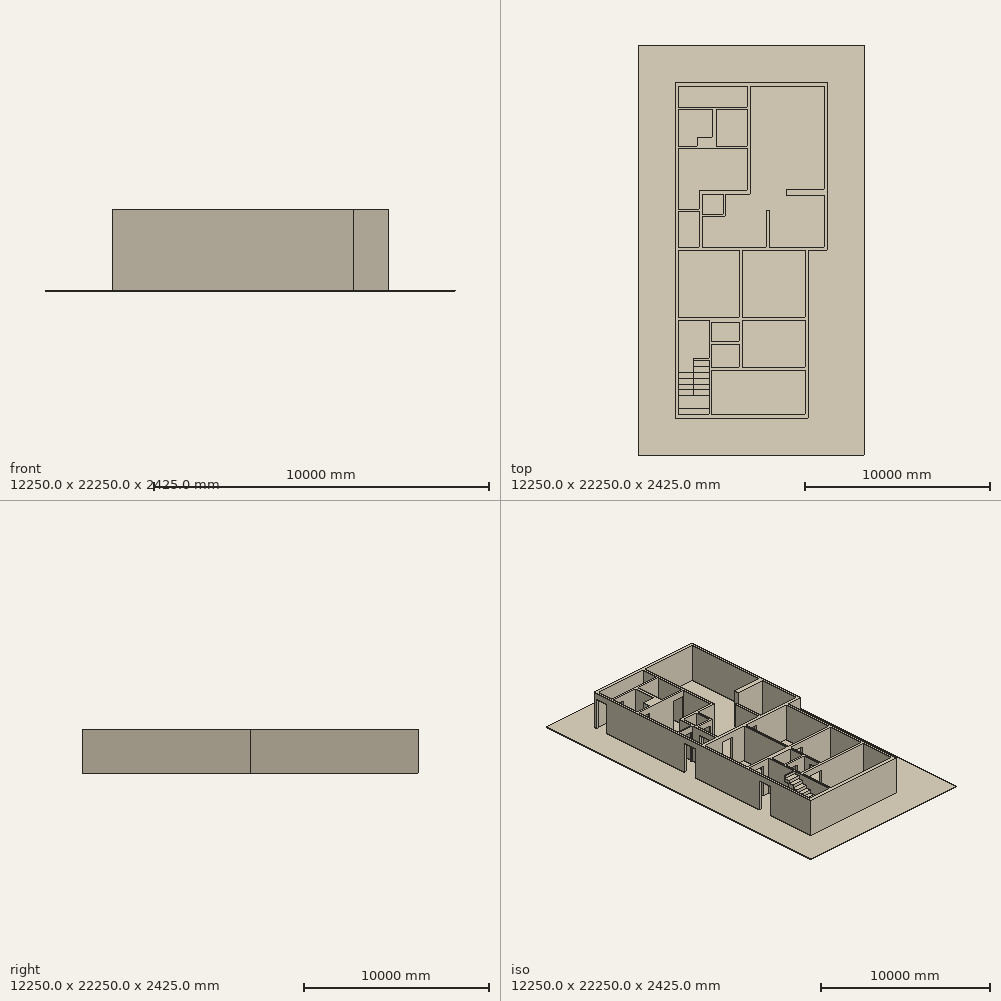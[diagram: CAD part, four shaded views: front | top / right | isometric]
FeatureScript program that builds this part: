
annotation { "Feature Type Name" : "Feature", "Feature Type Description" : "" }
export const myFeature = defineFeature(function(context is Context, id is Id, definition is map)
    precondition{}
    {
        {
            var Q0;
            Q0=qCreatedBy(makeId("Top.planeOp"),FACE);
            var sketch = newSketch(context, id + "F0", { "sketchPlane" : qUnion([Q0])});
            skLineSegment(sketch, "E0.bottom", {"start": v(-4125, 0) * mm, "end": v(4125, 0) * mm});
            skLineSegment(sketch, "E0.top", {"start": v(-3955, -9150) * mm, "end": v(-655, -9150) * mm});
            skLineSegment(sketch, "E0.left", {"start": v(-4125, 0) * mm, "end": v(-4125, -9150) * mm});
            skLineSegment(sketch, "E0.right", {"start": v(4125, 0) * mm, "end": v(4125, -9150) * mm});
            skLineSegment(sketch, "E1.bottom", {"start": v(-4125, -18250) * mm, "end": v(3075, -18250) * mm});
            skLineSegment(sketch, "E1.left", {"start": v(-4125, -18250) * mm, "end": v(-4125, -9150) * mm});
            skLineSegment(sketch, "E1.right", {"start": v(3075, -18250) * mm, "end": v(3075, -9150) * mm});
            skLineSegment(sketch, "E2.bottom", {"start": v(-3955, -200) * mm, "end": v(-195, -200) * mm});
            skLineSegment(sketch, "E2.top", {"start": v(-3955, -1340) * mm, "end": v(-195, -1340) * mm});
            skLineSegment(sketch, "E2.left", {"start": v(-3955, -200) * mm, "end": v(-3955, -1340) * mm});
            skLineSegment(sketch, "E2.right", {"start": v(-195, -200) * mm, "end": v(-195, -1340) * mm});
            skLineSegment(sketch, "E3.bottom", {"start": v(-3955, -1490) * mm, "end": v(-2105, -1490) * mm});
            skLineSegment(sketch, "E3.top", {"start": v(-3955, -3500) * mm, "end": v(-2105, -3500) * mm});
            skLineSegment(sketch, "E3.left", {"start": v(-3955, -1490) * mm, "end": v(-3955, -3500) * mm});
            skLineSegment(sketch, "E3.right", {"start": v(-2105, -1490) * mm, "end": v(-2105, -3500) * mm});
            skLineSegment(sketch, "E4.bottom", {"start": v(-1905, -1490) * mm, "end": v(-195, -1490) * mm});
            skLineSegment(sketch, "E4.top", {"start": v(-1905, -3500) * mm, "end": v(-195, -3500) * mm});
            skLineSegment(sketch, "E4.left", {"start": v(-1905, -1490) * mm, "end": v(-1905, -3500) * mm});
            skLineSegment(sketch, "E5.bottom", {"start": v(-3955, -3615) * mm, "end": v(-195, -3615) * mm});
            skLineSegment(sketch, "E5.top", {"start": v(-2825, -5885) * mm, "end": v(-195, -5885) * mm});
            skLineSegment(sketch, "E5.left", {"start": v(-3955, -3615) * mm, "end": v(-3955, -5885) * mm});
            skLineSegment(sketch, "E5.right", {"start": v(-195, -3615) * mm, "end": v(-195, -5885) * mm});
            skLineSegment(sketch, "E6.bottom", {"start": v(-2825, -6885) * mm, "end": v(-3955, -6885) * mm});
            skLineSegment(sketch, "E6.left", {"start": v(-2825, -6885) * mm, "end": v(-2825, -5885) * mm});
            skLineSegment(sketch, "E6.right", {"start": v(-3955, -6885) * mm, "end": v(-3955, -5885) * mm});
            skLineSegment(sketch, "E7.bottom", {"start": v(-3955, -8950) * mm, "end": v(-2825, -8950) * mm});
            skLineSegment(sketch, "E7.top", {"start": v(-3955, -7000) * mm, "end": v(-2825, -7000) * mm});
            skLineSegment(sketch, "E7.left", {"start": v(-3955, -8950) * mm, "end": v(-3955, -7000) * mm});
            skLineSegment(sketch, "E7.right", {"start": v(-2825, -8950) * mm, "end": v(-2825, -7000) * mm});
            skLineSegment(sketch, "E8.bottom", {"start": v(-2665, -6070) * mm, "end": v(-1545, -6070) * mm});
            skLineSegment(sketch, "E8.top", {"start": v(-2665, -7170) * mm, "end": v(-1545, -7170) * mm});
            skLineSegment(sketch, "E8.left", {"start": v(-2665, -6070) * mm, "end": v(-2665, -7170) * mm});
            skLineSegment(sketch, "E8.right", {"start": v(-1545, -6070) * mm, "end": v(-1545, -7170) * mm});
            skLineSegment(sketch, "E9.bottom", {"start": v(-45, -200) * mm, "end": v(3955, -200) * mm});
            skLineSegment(sketch, "E9.top", {"start": v(1905, -5800) * mm, "end": v(3955, -5800) * mm});
            skLineSegment(sketch, "E9.right", {"start": v(3955, -200) * mm, "end": v(3955, -5800) * mm});
            skLineSegment(sketch, "E10.bottom", {"start": v(3955, -8950) * mm, "end": v(955, -8950) * mm});
            skLineSegment(sketch, "E10.top", {"start": v(3955, -6120) * mm, "end": v(1905, -6120) * mm});
            skLineSegment(sketch, "E10.left", {"start": v(3955, -8950) * mm, "end": v(3955, -6120) * mm});
            skLineSegment(sketch, "E10.right", {"start": v(955, -8950) * mm, "end": v(955, -6950) * mm});
            skLineSegment(sketch, "E11.bottom", {"start": v(805, -8950) * mm, "end": v(-2665, -8950) * mm});
            skLineSegment(sketch, "E11.top", {"start": v(-1415, -7270) * mm, "end": v(-2665, -7270) * mm});
            skLineSegment(sketch, "E11.right", {"start": v(-2665, -8950) * mm, "end": v(-2665, -7270) * mm});
            skLineSegment(sketch, "E12.left", {"start": v(-1415, -6070) * mm, "end": v(-1415, -7270) * mm});
            skLineSegment(sketch, "E13.top", {"start": v(-3955, -18000) * mm, "end": v(-2305, -18000) * mm});
            skLineSegment(sketch, "E14.bottom", {"start": v(-2175, -15650) * mm, "end": v(2905, -15650) * mm});
            skLineSegment(sketch, "E14.top", {"start": v(-2175, -18000) * mm, "end": v(2905, -18000) * mm});
            skLineSegment(sketch, "E14.left", {"start": v(-2175, -15650) * mm, "end": v(-2175, -18000) * mm});
            skLineSegment(sketch, "E14.right", {"start": v(2905, -15650) * mm, "end": v(2905, -18000) * mm});
            skLineSegment(sketch, "E15.bottom", {"start": v(-2175, -13050) * mm, "end": v(-625, -13050) * mm});
            skLineSegment(sketch, "E15.top", {"start": v(-2175, -14085) * mm, "end": v(-625, -14085) * mm});
            skLineSegment(sketch, "E15.left", {"start": v(-2175, -13050) * mm, "end": v(-2175, -14085) * mm});
            skLineSegment(sketch, "E15.right", {"start": v(-625, -13050) * mm, "end": v(-625, -14085) * mm});
            skLineSegment(sketch, "E16.bottom", {"start": v(-2175, -14200) * mm, "end": v(-625, -14200) * mm});
            skLineSegment(sketch, "E16.top", {"start": v(-2175, -15500) * mm, "end": v(-625, -15500) * mm});
            skLineSegment(sketch, "E16.left", {"start": v(-2175, -14200) * mm, "end": v(-2175, -15500) * mm});
            skLineSegment(sketch, "E16.right", {"start": v(-625, -14200) * mm, "end": v(-625, -15500) * mm});
            skLineSegment(sketch, "E17.bottom", {"start": v(-495, -12900) * mm, "end": v(2905, -12900) * mm});
            skLineSegment(sketch, "E17.top", {"start": v(-495, -15500) * mm, "end": v(2905, -15500) * mm});
            skLineSegment(sketch, "E17.left", {"start": v(-495, -12900) * mm, "end": v(-495, -15500) * mm});
            skLineSegment(sketch, "E17.right", {"start": v(2905, -12900) * mm, "end": v(2905, -15500) * mm});
            skLineSegment(sketch, "E18.bottom", {"start": v(-3955, -12900) * mm, "end": v(-2305, -12900) * mm});
            skLineSegment(sketch, "E19.bottom", {"start": v(-3955, -12750) * mm, "end": v(-655, -12750) * mm});
            skLineSegment(sketch, "E19.left", {"start": v(-3955, -12750) * mm, "end": v(-3955, -9150) * mm});
            skLineSegment(sketch, "E19.right", {"start": v(-655, -12750) * mm, "end": v(-655, -9150) * mm});
            skLineSegment(sketch, "E20.bottom", {"start": v(-495, -12750) * mm, "end": v(2905, -12750) * mm});
            skLineSegment(sketch, "E20.top", {"start": v(-495, -9150) * mm, "end": v(2905, -9150) * mm});
            skLineSegment(sketch, "E20.left", {"start": v(-495, -12750) * mm, "end": v(-495, -9150) * mm});
            skLineSegment(sketch, "E20.right", {"start": v(2905, -12750) * mm, "end": v(2905, -9150) * mm});
            skLineSegment(sketch, "E21.trimOffspring", {"start": v(-495, -9150) * mm, "end": v(3075, -9150) * mm});
            skLineSegment(sketch, "E22.trimOffspring", {"start": v(-495, -9150) * mm, "end": v(4125, -9150) * mm});
            skLineSegment(sketch, "E23", {"start": v(-2955, -3500) * mm, "end": v(-2955, -2970) * mm});
            skLineSegment(sketch, "E24", {"start": v(-2955, -2970) * mm, "end": v(-2105, -2970) * mm});
            skLineSegment(sketch, "E25", {"start": v(-195, -1490) * mm, "end": v(-195, -3500) * mm});
            skLineSegment(sketch, "E26", {"start": v(805, -8950) * mm, "end": v(805, -6950) * mm});
            skLineSegment(sketch, "E27", {"start": v(805, -6950) * mm, "end": v(955, -6950) * mm});
            skLineSegment(sketch, "E28", {"start": v(1905, -6120) * mm, "end": v(1905, -5800) * mm});
            skLineSegment(sketch, "E29", {"start": v(-1415, -6070) * mm, "end": v(-45, -6070) * mm});
            skLineSegment(sketch, "E30", {"start": v(-45, -6070) * mm, "end": v(-45, -200) * mm});
            skLineSegment(sketch, "E31", {"start": v(-2305, -12900) * mm, "end": v(-2305, -18000) * mm});
            skLineSegment(sketch, "E32", {"start": v(-3955, -18000) * mm, "end": v(-3955, -12900) * mm});
            skPoint(sketch, "E33.endSnap0", {"position": v(-3130, -18000) * mm});
            skSolve(sketch);
        }
        {
            var Q0;
            Q0=makeQuery(id+"F0.imprint","IMPRINT",FACE,{"disambiguationData":[TD([[makeQuery(id+"F0.imprint","IMPRINT",EDGE,{"derivedFrom":sQuery(id+"F0.wireOp",EDGE,"E0.bottom")}),-1.0]])]});
            var Q1;
            {var subQ3=sQuery(id+"F0.wireOp",EDGE,"E23");Q1=makeQuery(id+"F0.imprint","IMPRINT",FACE,{"disambiguationData":[TD([[makeQuery(id+"F0.imprint","IMPRINT",EDGE,{"derivedFrom":subQ3}),-1.0]])]});}
            extrude(context, id + "F1", {"entities" : qUnion([Q0, Q1]), "depth" : 2400 * mm});
        }
        {
            var Q0;
            Q0=makeQuery(id+"F1.opExtrude","CAP_FACE",FACE,{"disambiguationData":[OSD([sQuery(id+"F0.wireOp",EDGE,"E0.bottom"),sQuery(id+"F0.wireOp",EDGE,"E0.left"),sQuery(id+"F0.wireOp",EDGE,"E0.right"),sQuery(id+"F0.wireOp",EDGE,"E1.bottom"),sQuery(id+"F0.wireOp",EDGE,"E1.left"),sQuery(id+"F0.wireOp",EDGE,"E1.right"),sQuery(id+"F0.wireOp",EDGE,"E2.bottom"),sQuery(id+"F0.wireOp",EDGE,"E2.top"),sQuery(id+"F0.wireOp",EDGE,"E2.left"),sQuery(id+"F0.wireOp",EDGE,"E2.right"),sQuery(id+"F0.wireOp",EDGE,"E3.bottom"),sQuery(id+"F0.wireOp",EDGE,"E3.top"),sQuery(id+"F0.wireOp",EDGE,"E3.left"),sQuery(id+"F0.wireOp",EDGE,"E3.right"),sQuery(id+"F0.wireOp",EDGE,"E4.bottom"),sQuery(id+"F0.wireOp",EDGE,"E4.top"),sQuery(id+"F0.wireOp",EDGE,"E4.left"),sQuery(id+"F0.wireOp",EDGE,"E5.bottom"),sQuery(id+"F0.wireOp",EDGE,"E5.top"),sQuery(id+"F0.wireOp",EDGE,"E5.left"),sQuery(id+"F0.wireOp",EDGE,"E5.right"),sQuery(id+"F0.wireOp",EDGE,"E6.bottom"),sQuery(id+"F0.wireOp",EDGE,"E6.left"),sQuery(id+"F0.wireOp",EDGE,"E6.right"),sQuery(id+"F0.wireOp",EDGE,"E7.bottom"),sQuery(id+"F0.wireOp",EDGE,"E7.top"),sQuery(id+"F0.wireOp",EDGE,"E7.left"),sQuery(id+"F0.wireOp",EDGE,"E7.right"),sQuery(id+"F0.wireOp",EDGE,"E8.bottom"),sQuery(id+"F0.wireOp",EDGE,"E8.top"),sQuery(id+"F0.wireOp",EDGE,"E8.left"),sQuery(id+"F0.wireOp",EDGE,"E8.right"),sQuery(id+"F0.wireOp",EDGE,"E9.bottom"),sQuery(id+"F0.wireOp",EDGE,"E9.top"),sQuery(id+"F0.wireOp",EDGE,"E9.right"),sQuery(id+"F0.wireOp",EDGE,"E10.bottom"),sQuery(id+"F0.wireOp",EDGE,"E10.top"),sQuery(id+"F0.wireOp",EDGE,"E10.left"),sQuery(id+"F0.wireOp",EDGE,"E10.right"),sQuery(id+"F0.wireOp",EDGE,"E11.bottom"),sQuery(id+"F0.wireOp",EDGE,"E11.top"),sQuery(id+"F0.wireOp",EDGE,"E11.right"),sQuery(id+"F0.wireOp",EDGE,"E12.left"),sQuery(id+"F0.wireOp",EDGE,"E13.bottom"),sQuery(id+"F0.wireOp",EDGE,"E13.top"),sQuery(id+"F0.wireOp",EDGE,"E13.left"),sQuery(id+"F0.wireOp",EDGE,"E13.right"),sQuery(id+"F0.wireOp",EDGE,"E14.bottom"),sQuery(id+"F0.wireOp",EDGE,"E14.top"),sQuery(id+"F0.wireOp",EDGE,"E14.left"),sQuery(id+"F0.wireOp",EDGE,"E14.right"),sQuery(id+"F0.wireOp",EDGE,"E15.bottom"),sQuery(id+"F0.wireOp",EDGE,"E15.top"),sQuery(id+"F0.wireOp",EDGE,"E15.left"),sQuery(id+"F0.wireOp",EDGE,"E15.right"),sQuery(id+"F0.wireOp",EDGE,"E16.bottom"),sQuery(id+"F0.wireOp",EDGE,"E16.top"),sQuery(id+"F0.wireOp",EDGE,"E16.left"),sQuery(id+"F0.wireOp",EDGE,"E16.right"),sQuery(id+"F0.wireOp",EDGE,"E17.bottom"),sQuery(id+"F0.wireOp",EDGE,"E17.top"),sQuery(id+"F0.wireOp",EDGE,"E17.left"),sQuery(id+"F0.wireOp",EDGE,"E17.right"),sQuery(id+"F0.wireOp",EDGE,"E18.bottom"),sQuery(id+"F0.wireOp",EDGE,"E18.top"),sQuery(id+"F0.wireOp",EDGE,"E18.left"),sQuery(id+"F0.wireOp",EDGE,"E18.right"),sQuery(id+"F0.wireOp",EDGE,"E19.bottom"),sQuery(id+"F0.wireOp",EDGE,"E0.top"),sQuery(id+"F0.wireOp",EDGE,"E19.left"),sQuery(id+"F0.wireOp",EDGE,"E19.right"),sQuery(id+"F0.wireOp",EDGE,"E20.bottom"),sQuery(id+"F0.wireOp",EDGE,"E20.left"),sQuery(id+"F0.wireOp",EDGE,"E20.right"),sQuery(id+"F0.wireOp",EDGE,"E22.trimOffspring"),sQuery(id+"F0.wireOp",EDGE,"E25"),sQuery(id+"F0.wireOp",EDGE,"E26"),sQuery(id+"F0.wireOp",EDGE,"E27"),sQuery(id+"F0.wireOp",EDGE,"E28"),sQuery(id+"F0.wireOp",EDGE,"E29"),sQuery(id+"F0.wireOp",EDGE,"E30")])],"isStart":false});
            var sketch = newSketch(context, id + "F2", { "sketchPlane" : qUnion([Q0])});
            skLineSegment(sketch, "E34", {"start": v(-1575, -15500) * mm, "end": v(-1575, -15650) * mm});
            skLineSegment(sketch, "E35", {"start": v(-1575, -15650) * mm, "end": v(-675, -15650) * mm});
            skLineSegment(sketch, "E36", {"start": v(-675, -15650) * mm, "end": v(-675, -15500) * mm});
            skLineSegment(sketch, "E37", {"start": v(-625, -15480) * mm, "end": v(-495, -15480) * mm});
            skLineSegment(sketch, "E38", {"start": v(-495, -14600) * mm, "end": v(-625, -14600) * mm});
            skLineSegment(sketch, "E39", {"start": v(-2175, -15400) * mm, "end": v(-2305, -15400) * mm});
            skLineSegment(sketch, "E40", {"start": v(-2025, -14200) * mm, "end": v(-2025, -14085) * mm});
            skLineSegment(sketch, "E41", {"start": v(-2025, -14085) * mm, "end": v(-1225, -14085) * mm});
            skLineSegment(sketch, "E42", {"start": v(-1225, -14085) * mm, "end": v(-1225, -14200) * mm});
            skLineSegment(sketch, "E43", {"start": v(-345, -12750) * mm, "end": v(-345, -12900) * mm});
            skLineSegment(sketch, "E44", {"start": v(-345, -12900) * mm, "end": v(505, -12900) * mm});
            skLineSegment(sketch, "E45", {"start": v(505, -12900) * mm, "end": v(505, -12750) * mm});
            skLineSegment(sketch, "E46", {"start": v(-445, -8950) * mm, "end": v(-445, -9150) * mm});
            skLineSegment(sketch, "E47", {"start": v(-445, -9150) * mm, "end": v(405, -9150) * mm});
            skLineSegment(sketch, "E48", {"start": v(405, -9150) * mm, "end": v(405, -8950) * mm});
            skLineSegment(sketch, "E49", {"start": v(-1615, -8950) * mm, "end": v(-1615, -9150) * mm});
            skLineSegment(sketch, "E50", {"start": v(-1615, -9150) * mm, "end": v(-2465, -9150) * mm});
            skLineSegment(sketch, "E51", {"start": v(-2465, -9150) * mm, "end": v(-2465, -8950) * mm});
            skLineSegment(sketch, "E52", {"start": v(-2665, -7570) * mm, "end": v(-2825, -7570) * mm});
            skLineSegment(sketch, "E53", {"start": v(-2825, -7570) * mm, "end": v(-2825, -8450) * mm});
            skLineSegment(sketch, "E54", {"start": v(-2825, -8450) * mm, "end": v(-2665, -8450) * mm});
            skLineSegment(sketch, "E55", {"start": v(-2215, -7170) * mm, "end": v(-2215, -7270) * mm});
            skLineSegment(sketch, "E56", {"start": v(-2215, -7270) * mm, "end": v(-1565, -7270) * mm});
            skLineSegment(sketch, "E57", {"start": v(-1565, -7270) * mm, "end": v(-1565, -7170) * mm});
            skLineSegment(sketch, "E58", {"start": v(-3755, -6885) * mm, "end": v(-3755, -7000) * mm});
            skLineSegment(sketch, "E59", {"start": v(-3755, -7000) * mm, "end": v(-2905, -7000) * mm});
            skLineSegment(sketch, "E60", {"start": v(-2905, -7000) * mm, "end": v(-2905, -6885) * mm});
            skLineSegment(sketch, "E61", {"start": v(-3655, -12750) * mm, "end": v(-3655, -12900) * mm});
            skLineSegment(sketch, "E62", {"start": v(-3655, -12900) * mm, "end": v(-2805, -12900) * mm});
            skLineSegment(sketch, "E63", {"start": v(-2805, -12900) * mm, "end": v(-2805, -12750) * mm});
            skLineSegment(sketch, "E64", {"start": v(-205, -3500) * mm, "end": v(-205, -3615) * mm});
            skLineSegment(sketch, "E65", {"start": v(-205, -3615) * mm, "end": v(-1075, -3615) * mm});
            skLineSegment(sketch, "E66", {"start": v(-1075, -3615) * mm, "end": v(-1075, -3500) * mm});
            skLineSegment(sketch, "E67", {"start": v(-3935, -3500) * mm, "end": v(-3935, -3615) * mm});
            skLineSegment(sketch, "E68", {"start": v(-3935, -3615) * mm, "end": v(-3055, -3615) * mm});
            skLineSegment(sketch, "E69", {"start": v(-3055, -3615) * mm, "end": v(-3055, -1490) * mm});
            skLineSegment(sketch, "E70", {"start": v(-3935, -1340) * mm, "end": v(-3935, -1490) * mm});
            skLineSegment(sketch, "E71", {"start": v(-3935, -1490) * mm, "end": v(-3135, -1490) * mm});
            skLineSegment(sketch, "E72", {"start": v(-3135, -1490) * mm, "end": v(-3135, -1340) * mm});
            skLineSegment(sketch, "E73", {"start": v(-4125, -7620) * mm, "end": v(-3955, -7620) * mm});
            skLineSegment(sketch, "E74", {"start": v(-3955, -7620) * mm, "end": v(-3955, -8500) * mm});
            skLineSegment(sketch, "E75", {"start": v(-3955, -8500) * mm, "end": v(-4125, -8500) * mm});
            skLineSegment(sketch, "E76", {"start": v(-3955, -240) * mm, "end": v(-4125, -240) * mm});
            skLineSegment(sketch, "E77", {"start": v(-4125, -240) * mm, "end": v(-4125, -1090) * mm});
            skLineSegment(sketch, "E78", {"start": v(-4125, -1090) * mm, "end": v(-3955, -1090) * mm});
            skLineSegment(sketch, "E79", {"start": v(-2305, -14520) * mm, "end": v(-2175, -14520) * mm});
            skLineSegment(sketch, "E80", {"start": v(-2175, -14520) * mm, "end": v(-2175, -15400) * mm});
            skLineSegment(sketch, "E81", {"start": v(-4125, -13950) * mm, "end": v(-3955, -13950) * mm});
            skLineSegment(sketch, "E82", {"start": v(-3955, -13950) * mm, "end": v(-3955, -14830) * mm});
            skLineSegment(sketch, "E83", {"start": v(-3955, -14830) * mm, "end": v(-4125, -14830) * mm});
            skSolve(sketch);
        }
        {
            var Q0;
            {var subQ0=sQuery(id+"F2.wireOp",EDGE,"E76");Q0=makeQuery(id+"F2.imprint","IMPRINT",FACE,{"disambiguationData":[TD([[makeQuery(id+"F2.imprint","IMPRINT",EDGE,{"derivedFrom":subQ0}),1.0]])]});}
            var Q1;
            {var subQ0=sQuery(id+"F2.wireOp",EDGE,"E70");Q1=makeQuery(id+"F2.imprint","IMPRINT",FACE,{"disambiguationData":[TD([[makeQuery(id+"F2.imprint","IMPRINT",EDGE,{"derivedFrom":subQ0}),1.0]])]});}
            var Q2;
            {var subQ0=sQuery(id+"F2.wireOp",EDGE,"E67");Q2=makeQuery(id+"F2.imprint","IMPRINT",FACE,{"disambiguationData":[TD([[makeQuery(id+"F2.imprint","IMPRINT",EDGE,{"derivedFrom":subQ0}),1.0]])]});}
            var Q3;
            {var subQ0=sQuery(id+"F2.wireOp",EDGE,"E64");Q3=makeQuery(id+"F2.imprint","IMPRINT",FACE,{"disambiguationData":[TD([[makeQuery(id+"F2.imprint","IMPRINT",EDGE,{"derivedFrom":subQ0}),-1.0]])]});}
            var Q4;
            {var subQ0=sQuery(id+"F2.wireOp",EDGE,"E58");Q4=makeQuery(id+"F2.imprint","IMPRINT",FACE,{"disambiguationData":[TD([[makeQuery(id+"F2.imprint","IMPRINT",EDGE,{"derivedFrom":subQ0}),1.0]])]});}
            var Q5;
            {var subQ0=sQuery(id+"F2.wireOp",EDGE,"E73");Q5=makeQuery(id+"F2.imprint","IMPRINT",FACE,{"disambiguationData":[TD([[makeQuery(id+"F2.imprint","IMPRINT",EDGE,{"derivedFrom":subQ0}),-1.0]])]});}
            var Q6;
            {var subQ0=sQuery(id+"F2.wireOp",EDGE,"E55");Q6=makeQuery(id+"F2.imprint","IMPRINT",FACE,{"disambiguationData":[TD([[makeQuery(id+"F2.imprint","IMPRINT",EDGE,{"derivedFrom":subQ0}),1.0]])]});}
            var Q7;
            {var subQ0=sQuery(id+"F2.wireOp",EDGE,"E52");Q7=makeQuery(id+"F2.imprint","IMPRINT",FACE,{"disambiguationData":[TD([[makeQuery(id+"F2.imprint","IMPRINT",EDGE,{"derivedFrom":subQ0}),1.0]])]});}
            var Q8;
            {var subQ0=sQuery(id+"F2.wireOp",EDGE,"E49");Q8=makeQuery(id+"F2.imprint","IMPRINT",FACE,{"disambiguationData":[TD([[makeQuery(id+"F2.imprint","IMPRINT",EDGE,{"derivedFrom":subQ0}),-1.0]])]});}
            var Q9;
            {var subQ0=sQuery(id+"F2.wireOp",EDGE,"E46");Q9=makeQuery(id+"F2.imprint","IMPRINT",FACE,{"disambiguationData":[TD([[makeQuery(id+"F2.imprint","IMPRINT",EDGE,{"derivedFrom":subQ0}),1.0]])]});}
            var Q10;
            {var subQ0=sQuery(id+"F2.wireOp",EDGE,"E61");Q10=makeQuery(id+"F2.imprint","IMPRINT",FACE,{"disambiguationData":[TD([[makeQuery(id+"F2.imprint","IMPRINT",EDGE,{"derivedFrom":subQ0}),1.0]])]});}
            var Q11;
            {var subQ0=sQuery(id+"F2.wireOp",EDGE,"E43");Q11=makeQuery(id+"F2.imprint","IMPRINT",FACE,{"disambiguationData":[TD([[makeQuery(id+"F2.imprint","IMPRINT",EDGE,{"derivedFrom":subQ0}),1.0]])]});}
            var Q12;
            {var subQ0=sQuery(id+"F2.wireOp",EDGE,"E40");Q12=makeQuery(id+"F2.imprint","IMPRINT",FACE,{"disambiguationData":[TD([[makeQuery(id+"F2.imprint","IMPRINT",EDGE,{"derivedFrom":subQ0}),-1.0]])]});}
            var Q13;
            {var subQ0=sQuery(id+"F2.wireOp",EDGE,"E37");Q13=makeQuery(id+"F2.imprint","IMPRINT",FACE,{"disambiguationData":[TD([[makeQuery(id+"F2.imprint","IMPRINT",EDGE,{"derivedFrom":subQ0}),1.0]])]});}
            var Q14;
            {var subQ0=sQuery(id+"F2.wireOp",EDGE,"E34");Q14=makeQuery(id+"F2.imprint","IMPRINT",FACE,{"disambiguationData":[TD([[makeQuery(id+"F2.imprint","IMPRINT",EDGE,{"derivedFrom":subQ0}),1.0]])]});}
            var Q15;
            {var subQ0=sQuery(id+"F2.wireOp",EDGE,"E39");Q15=makeQuery(id+"F2.imprint","IMPRINT",FACE,{"disambiguationData":[TD([[makeQuery(id+"F2.imprint","IMPRINT",EDGE,{"derivedFrom":subQ0}),-1.0]])]});}
            var Q16;
            {var subQ0=sQuery(id+"F2.wireOp",EDGE,"E81");Q16=makeQuery(id+"F2.imprint","IMPRINT",FACE,{"disambiguationData":[TD([[makeQuery(id+"F2.imprint","IMPRINT",EDGE,{"derivedFrom":subQ0}),-1.0]])]});}
            extrude(context, id + "F3", {"entities" : qUnion([Q0, Q1, Q2, Q3, Q4, Q5, Q6, Q7, Q8, Q9, Q10, Q11, Q12, Q13, Q14, Q15, Q16]), "operationType" : NewBodyOperationType.REMOVE, "endBound" : BoundingType.UP_TO_NEXT, "oppositeDirection" : true, "depth" : 2200 * mm, "hasSecondDirection" : true, "secondDirectionOppositeDirection" : true, "secondDirectionDepth" : 400 * mm});
        }
        {
            var Q0;
            Q0=qCreatedBy(makeId("Top.planeOp"),FACE);
            var sketch = newSketch(context, id + "F4", { "sketchPlane" : qUnion([Q0])});
            skLineSegment(sketch, "E84.bottom", {"start": v(6125, -20250) * mm, "end": v(-6125, -20250) * mm});
            skLineSegment(sketch, "E84.top", {"start": v(6125, 2000) * mm, "end": v(-6125, 2000) * mm});
            skLineSegment(sketch, "E84.left", {"start": v(6125, -20250) * mm, "end": v(6125, 2000) * mm});
            skLineSegment(sketch, "E84.right", {"start": v(-6125, -20250) * mm, "end": v(-6125, 2000) * mm});
            skSolve(sketch);
        }
        {
            var Q0;
            Q0 = qSketchRegion(id + "F4", true);
            extrude(context, id + "F5", {"entities" : qUnion([Q0]), "oppositeDirection" : true, "depth" : 25 * mm});
        }
        {
            var Q0;
            Q0=makeQuery(id+"F1.opExtrude","SWEPT_FACE",FACE,{"disambiguationData":[OSD([sQuery(id+"F0.wireOp",EDGE,"E31")])]});
            var sketch = newSketch(context, id + "F6", { "sketchPlane" : qUnion([Q0])});
            skLineSegment(sketch, "E85", {"start": v(15730, 220) * mm, "end": v(16050, 220) * mm});
            skLineSegment(sketch, "E86", {"start": v(16050, 220) * mm, "end": v(16050, 420) * mm});
            skLineSegment(sketch, "E87", {"start": v(16050, 420) * mm, "end": v(16370, 420) * mm});
            skLineSegment(sketch, "E88", {"start": v(16370, 420) * mm, "end": v(16370, 620) * mm});
            skLineSegment(sketch, "E89", {"start": v(16370, 620) * mm, "end": v(16690, 620) * mm});
            skLineSegment(sketch, "E90", {"start": v(16690, 620) * mm, "end": v(16690, 820) * mm});
            skLineSegment(sketch, "E91", {"start": v(16690, 820) * mm, "end": v(17010, 820) * mm});
            skLineSegment(sketch, "E92", {"start": v(17010, 820) * mm, "end": v(17010, 1020) * mm});
            skLineSegment(sketch, "E93", {"start": v(15730, 220) * mm, "end": v(15730, 0) * mm});
            skLineSegment(sketch, "E94", {"start": v(17010, 1020) * mm, "end": v(17680, 1020) * mm});
            skLineSegment(sketch, "E95", {"start": v(17680, 1020) * mm, "end": v(17680, 0) * mm});
            skLineSegment(sketch, "E96", {"start": v(17010, 1020) * mm, "end": v(17010, 1220) * mm});
            skLineSegment(sketch, "E97", {"start": v(17010, 1220) * mm, "end": v(16690, 1220) * mm});
            skLineSegment(sketch, "E98", {"start": v(16690, 1220) * mm, "end": v(16690, 1420) * mm});
            skLineSegment(sketch, "E99", {"start": v(16690, 1420) * mm, "end": v(16370, 1420) * mm});
            skLineSegment(sketch, "E100", {"start": v(16370, 1420) * mm, "end": v(16370, 1620) * mm});
            skLineSegment(sketch, "E101", {"start": v(16370, 1620) * mm, "end": v(16068, 1620) * mm});
            skLineSegment(sketch, "E102", {"start": v(16068, 1620) * mm, "end": v(16068, 1820) * mm});
            skLineSegment(sketch, "E103", {"start": v(16068, 1820) * mm, "end": v(15748, 1820) * mm});
            skLineSegment(sketch, "E104", {"start": v(15748, 1820) * mm, "end": v(15748, 2020) * mm});
            skLineSegment(sketch, "E105", {"start": v(15748, 2020) * mm, "end": v(15428, 2020) * mm});
            skLineSegment(sketch, "E106", {"start": v(15428, 2020) * mm, "end": v(15428, 2220) * mm});
            skLineSegment(sketch, "E107", {"start": v(15428, 2220) * mm, "end": v(15108, 2220) * mm});
            skLineSegment(sketch, "E108", {"start": v(15108, 2220) * mm, "end": v(15108, 2400) * mm});
            skLineSegment(sketch, "E109", {"start": v(15108, 2400) * mm, "end": v(15008, 2400) * mm});
            skLineSegment(sketch, "E110", {"start": v(15008, 2400) * mm, "end": v(15008, 2003.48) * mm});
            skLineSegment(sketch, "E111", {"start": v(15008, 2003.48) * mm, "end": v(16440.2, 1020) * mm});
            skLineSegment(sketch, "E112", {"start": v(17010, 820) * mm, "end": v(17680, 820) * mm});
            skLineSegment(sketch, "E113", {"start": v(16440.2, 1020) * mm, "end": v(17010, 990) * mm});
            skSolve(sketch);
        }
        {
            var Q0;
            Q0=makeQuery(id+"F6.imprint","IMPRINT",FACE,{"disambiguationData":[TD([[makeQuery(id+"F6.imprint","IMPRINT",EDGE,{"derivedFrom":sQuery(id+"F6.wireOp",EDGE,"E85")}),-1.0]])]});
            var Q1;
            Q1=makeQuery(id+"F6.imprint","IMPRINT",FACE,{"disambiguationData":[TD([[makeQuery(id+"F6.imprint","IMPRINT",EDGE,{"derivedFrom":sQuery(id+"F6.wireOp",EDGE,"E92")}),-1.0]])]});
            extrude(context, id + "F7", {"entities" : qUnion([Q0, Q1]), "depth" : 1650 * mm, "hasSecondDirection" : true, "secondDirectionOppositeDirection" : false, "secondDirectionDepth" : 825 * mm});
        }
        {
            var Q0;
            Q0=makeQuery(id+"F6.imprint","IMPRINT",FACE,{"disambiguationData":[TD([[makeQuery(id+"F6.imprint","IMPRINT",EDGE,{"derivedFrom":sQuery(id+"F6.wireOp",EDGE,"E96")}),1.0]])]});
            var Q1;
            Q1=makeQuery(id+"F6.imprint","IMPRINT",FACE,{"disambiguationData":[TD([[makeQuery(id+"F6.imprint","IMPRINT",EDGE,{"derivedFrom":sQuery(id+"F6.wireOp",EDGE,"E92")}),-1.0]])]});
            extrude(context, id + "F8", {"entities" : qUnion([Q0, Q1]), "operationType" : NewBodyOperationType.ADD, "depth" : 825 * mm});
        }
    });
